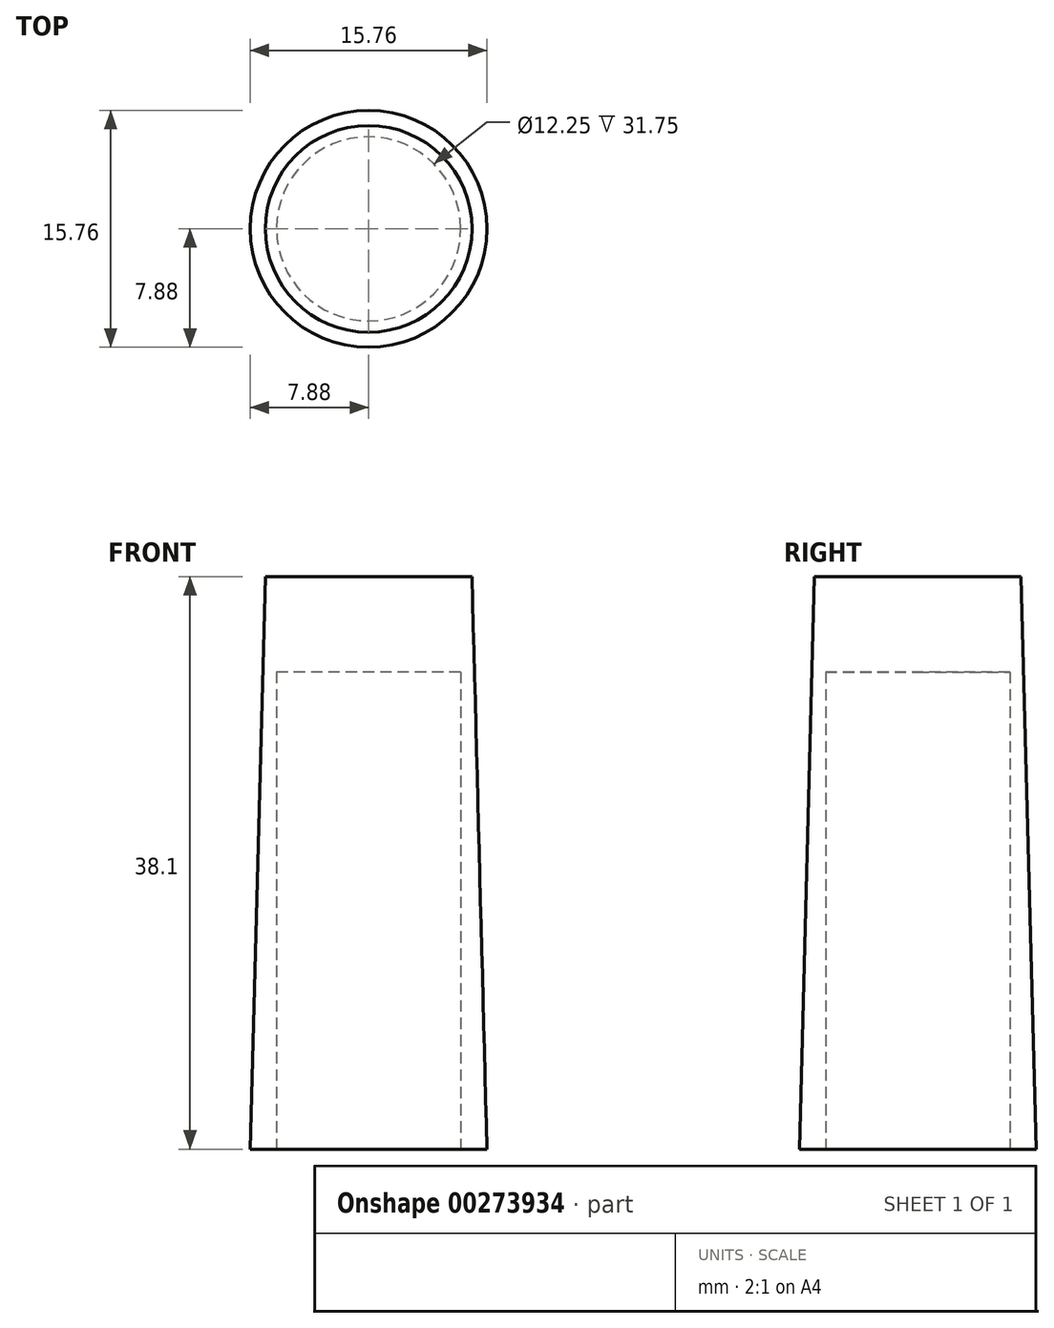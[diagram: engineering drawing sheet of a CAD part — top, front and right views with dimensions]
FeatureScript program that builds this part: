
annotation { "Feature Type Name" : "Feature", "Feature Type Description" : "" }
export const myFeature = defineFeature(function(context is Context, id is Id, definition is map)
    precondition{}
    {
        {
            var Q0;
            Q0=qCreatedBy(makeId("Top.planeOp"),FACE);
            var sketch = newSketch(context, id + "F0", { "sketchPlane" : qUnion([Q0])});
            skCircle(sketch, "E0", {"center": v(0, 0) * mm, "radius": 6.12 * mm});
            skCircle(sketch, "E1", {"center": v(0, 0) * mm, "radius": 7.88 * mm});
            skSolve(sketch);
        }
        {
            var Q0;
            Q0=makeQuery(id+"F0.imprint","IMPRINT",FACE,{"disambiguationData":[TD([[makeQuery(id+"F0.imprint","IMPRINT",EDGE,{"derivedFrom":sQuery(id+"F0.wireOp",EDGE,"E0")}),-1.0]])]});
            var Q1;
            Q1=makeQuery(id+"F0.imprint","IMPRINT",FACE,{"disambiguationData":[TD([[makeQuery(id+"F0.imprint","IMPRINT",EDGE,{"derivedFrom":sQuery(id+"F0.wireOp",EDGE,"E0")}),1.0]])]});
            extrude(context, id + "F1", {"entities" : qUnion([Q0, Q1]), "depth" : 38.1 * mm, "hasDraft" : true, "draftAngle" : 1.5 * degree, "draftPullDirection" : true});
        }
        {
            var Q0;
            Q0=makeQuery(id+"F0.imprint","IMPRINT",FACE,{"disambiguationData":[TD([[makeQuery(id+"F0.imprint","IMPRINT",EDGE,{"derivedFrom":sQuery(id+"F0.wireOp",EDGE,"E0")}),1.0]])]});
            extrude(context, id + "F2", {"entities" : qUnion([Q0]), "operationType" : NewBodyOperationType.REMOVE, "depth" : 31.75 * mm});
        }
    });
